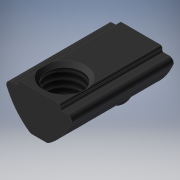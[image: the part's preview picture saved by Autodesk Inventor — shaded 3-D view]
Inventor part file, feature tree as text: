
AUTODESK INVENTOR PART (.ipt)
format: ipt  version: 2025 (Build 290162000, 162)  size: 209,408 bytes
history: native  units: mm
features: other x7, sketch x4, revolve x2, extrude x1, thread x1, hole x1
ambient origin geometry x8: Origin, YZ Plane, XZ Plane, XY Plane, X Axis, Y Axis, Z Axis, Center Point
bodies: Solid1 (feature_tree)
feature tree (16):
  extrude  "Extrusion1"  TaperAngle=360.0deg  [1 undecoded]
  revolve  "Revolution1"  Angle=360.0deg
  thread  "Thread1"  [1 undecoded]
  hole  "Hole1"  [1 undecoded]
  revolve  "Revolution2"  [1 undecoded]
  other  "nut_to_bolt_XY"
  other  "nut_to_bolt_YZ"
  other  "nut_to_bolt_ZX"
  other  "nut_to_bolt_X"
  other  "nut_to_bolt_Y"
  other  "nut_to_bolt_Z"
  other  "nut_to_bolt_Center"
  sketch  "Sketch_1"  dims[d0=12.0mm d1=0.0mm d2=360.0deg]
  sketch  "Sketch_2"  dims[d3=3.834mm d4=0.0mm]
  sketch  "Sketch3"  dims[d5=3.0mm d6=6.0mm d7=4.0mm d8=2.0mm d9=90.0deg d10=3.28mm d11=0.0mm d12=360.0deg]
  sketch  "Sketch_5"
note: 4 required parameter values undecoded (feature->parameter linkage not recoverable at this tier; creation-order binding heuristic only, values carry confidence <= 0.55)
